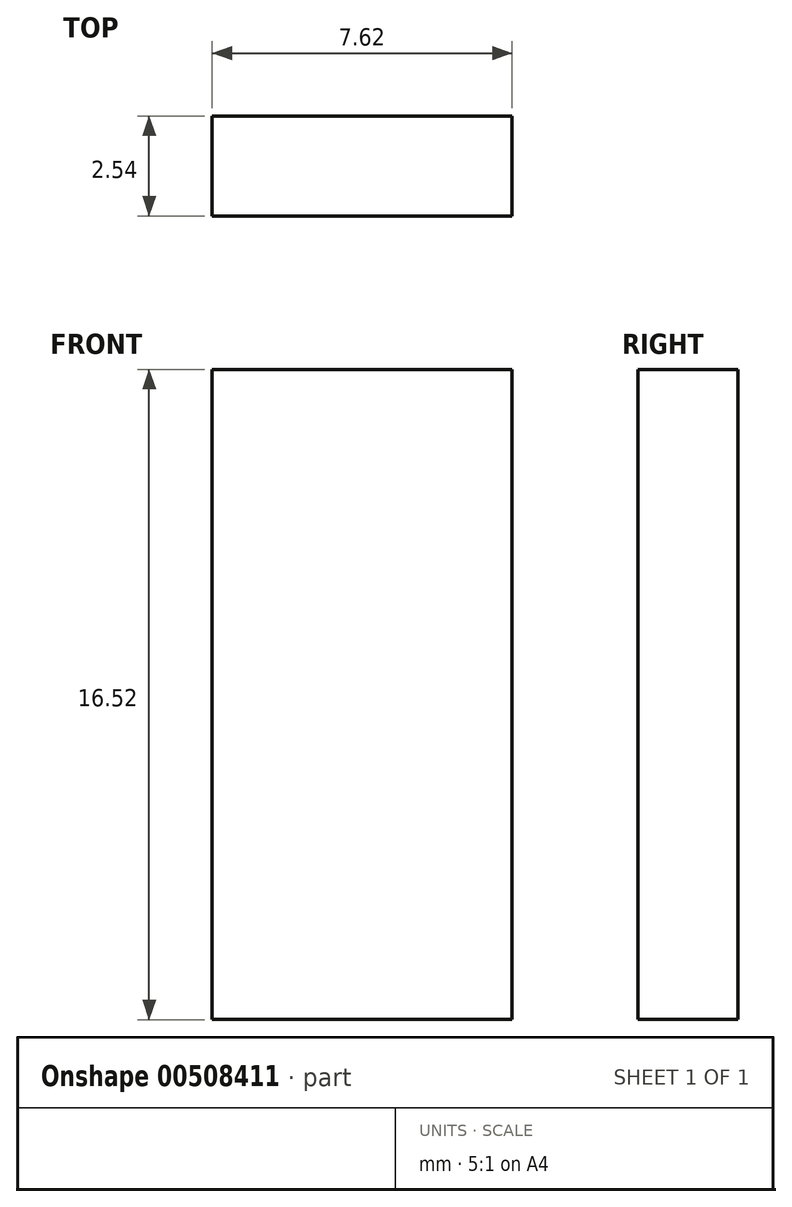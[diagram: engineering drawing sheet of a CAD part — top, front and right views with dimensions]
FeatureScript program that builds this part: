
annotation { "Feature Type Name" : "Feature", "Feature Type Description" : "" }
export const myFeature = defineFeature(function(context is Context, id is Id, definition is map)
    precondition{}
    {
        {
            var Q0;
            Q0=qCreatedBy(makeId("Front.planeOp"),FACE);
            var sketch = newSketch(context, id + "F0", { "sketchPlane" : qUnion([Q0])});
            skLineSegment(sketch, "E0.bottom", {"start": v(-3.8, 8.26) * mm, "end": v(3.81, 8.26) * mm});
            skLineSegment(sketch, "E0.top", {"start": v(-3.81, -8.26) * mm, "end": v(3.8, -8.26) * mm});
            skLineSegment(sketch, "E0.left", {"start": v(-3.8, 8.26) * mm, "end": v(-3.81, -8.26) * mm});
            skLineSegment(sketch, "E0.right", {"start": v(3.81, 8.26) * mm, "end": v(3.8, -8.26) * mm});
            skPoint(sketch, "E0.middle", {"position": v(0, 0) * mm});
            skSolve(sketch);
        }
        {
            var Q0;
            Q0=makeQuery(id+"F0.imprint","IMPRINT",FACE,{"disambiguationData":[TD([[makeQuery(id+"F0.imprint","IMPRINT",EDGE,{"derivedFrom":sQuery(id+"F0.wireOp",EDGE,"E0.bottom")}),-1.0]])]});
            extrude(context, id + "F1", {"entities" : qUnion([Q0]), "endBound" : BoundingType.SYMMETRIC, "depth" : 2.54 * mm});
        }
    });
